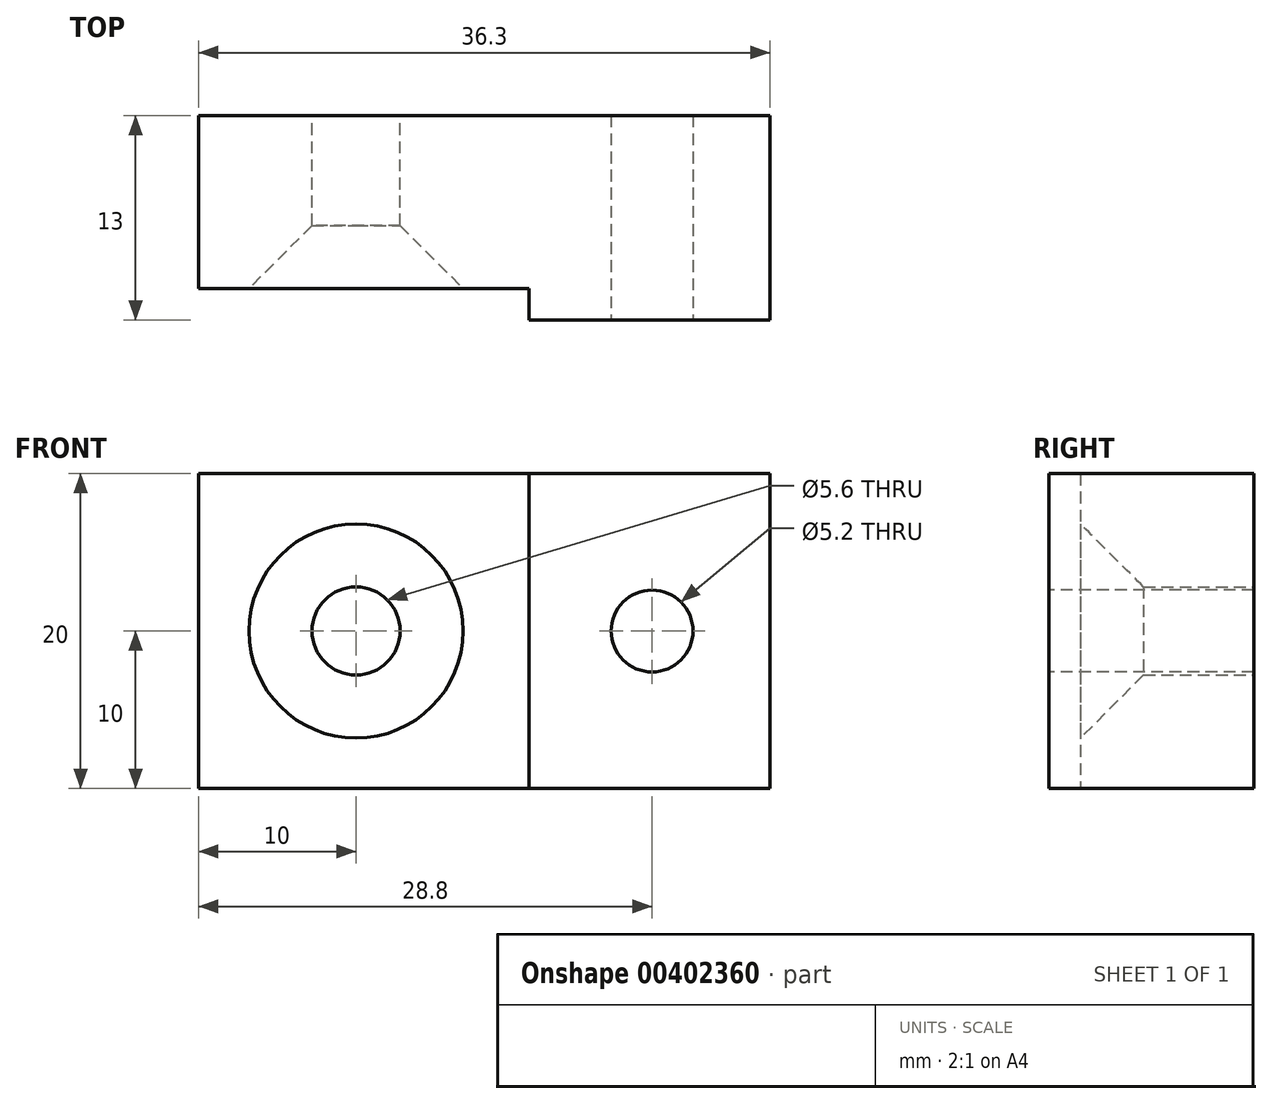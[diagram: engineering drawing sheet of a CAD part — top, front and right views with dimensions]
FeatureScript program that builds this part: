
annotation { "Feature Type Name" : "Feature", "Feature Type Description" : "" }
export const myFeature = defineFeature(function(context is Context, id is Id, definition is map)
    precondition{}
    {
        {
            var Q0;
            Q0=qCreatedBy(makeId("Top.planeOp"),FACE);
            var sketch = newSketch(context, id + "F0", { "sketchPlane" : qUnion([Q0])});
            skLineSegment(sketch, "E0", {"start": v(0, 20) * mm, "end": v(20, 20) * mm});
            skLineSegment(sketch, "E1", {"start": v(20, 20) * mm, "end": v(20, 31) * mm});
            skLineSegment(sketch, "E2", {"start": v(0, 20) * mm, "end": v(0, 31) * mm});
            skLineSegment(sketch, "E3", {"start": v(0, 31) * mm, "end": v(20, 31) * mm});
            skSolve(sketch);
        }
        {
            var Q0;
            Q0=makeQuery(id+"F0.imprint","IMPRINT",FACE,{"disambiguationData":[TD([[makeQuery(id+"F0.imprint","IMPRINT",EDGE,{"derivedFrom":sQuery(id+"F0.wireOp",EDGE,"xvJhXUSX-wpkq-VukB-ggIu-nVvylT8XI342")}),1.0]])]});
            var Q1;
            Q1=makeQuery(id+"F0.imprint","IMPRINT",FACE,{"disambiguationData":[TD([[makeQuery(id+"F0.imprint","IMPRINT",EDGE,{"derivedFrom":sQuery(id+"F0.wireOp",EDGE,"E0")}),1.0]])]});
            extrude(context, id + "F1", {"entities" : qUnion([Q0, Q1]), "depth" : 20 * mm});
        }
        {
            var Q0;
            Q0=makeQuery(id+"F1.opExtrude","SWEPT_FACE",FACE,{"disambiguationData":[OSD([sQuery(id+"F0.wireOp",EDGE,"E3")])]});
            var sketch = newSketch(context, id + "F2", { "sketchPlane" : qUnion([Q0])});
            skCircle(sketch, "E4", {"center": v(-10, 10) * mm, "radius": 2.8 * mm});
            skSolve(sketch);
        }
        {
            var Q0;
            Q0=makeQuery(id+"F2.imprint","IMPRINT",FACE,{"disambiguationData":[TD([[makeQuery(id+"F2.imprint","IMPRINT",EDGE,{"derivedFrom":sQuery(id+"F2.wireOp",EDGE,"E4")}),1.0]])]});
            extrude(context, id + "F3", {"entities" : qUnion([Q0]), "operationType" : NewBodyOperationType.REMOVE, "oppositeDirection" : true, "depth" : 25 * mm});
        }
        {
            var Q0;
            Q0=makeQuery(id+"F1.opExtrude","CAP_FACE",FACE,{"disambiguationData":[OSD([sQuery(id+"F0.wireOp",EDGE,"E0"),sQuery(id+"F0.wireOp",EDGE,"E1"),sQuery(id+"F0.wireOp",EDGE,"E2"),sQuery(id+"F0.wireOp",EDGE,"E3")])],"isStart":false});
            var sketch = newSketch(context, id + "F4", { "sketchPlane" : qUnion([Q0])});
            skLineSegment(sketch, "E5.top", {"start": v(21, 18) * mm, "end": v(36.3, 18) * mm});
            skLineSegment(sketch, "E5.left", {"start": v(20, 31) * mm, "end": v(20, 20) * mm});
            skLineSegment(sketch, "E5.right", {"start": v(36.3, 31) * mm, "end": v(36.3, 18) * mm});
            skLineSegment(sketch, "E6", {"start": v(20, 31) * mm, "end": v(36.3, 31) * mm});
            skLineSegment(sketch, "E7", {"start": v(20, 20) * mm, "end": v(21, 20) * mm});
            skLineSegment(sketch, "E8", {"start": v(21, 20) * mm, "end": v(21, 18) * mm});
            skSolve(sketch);
        }
        {
            var Q0;
            Q0=makeQuery(id+"F4.imprint","IMPRINT",FACE,{"disambiguationData":[TD([[makeQuery(id+"F4.imprint","IMPRINT",EDGE,{"derivedFrom":sQuery(id+"F4.wireOp",EDGE,"E5.top")}),1.0]])]});
            var Q1;
            Q1=makeQuery(id+"F1.opExtrude","CAP_FACE",FACE,{"disambiguationData":[OSD([sQuery(id+"F0.wireOp",EDGE,"E0"),sQuery(id+"F0.wireOp",EDGE,"E1"),sQuery(id+"F0.wireOp",EDGE,"E2"),sQuery(id+"F0.wireOp",EDGE,"E3")])],"isStart":true});
            extrude(context, id + "F5", {"entities" : qUnion([Q0]), "operationType" : NewBodyOperationType.ADD, "endBound" : BoundingType.UP_TO_SURFACE, "oppositeDirection" : true, "endBoundEntityFace" : qUnion([Q1]), "depth" : 6 * mm});
        }
        {
            var Q0;
            Q0=makeQuery(id+"F5.opExtrude","SWEPT_FACE",FACE,{"disambiguationData":[OSD([sQuery(id+"F4.wireOp",EDGE,"E5.top")])]});
            var sketch = newSketch(context, id + "F6", { "sketchPlane" : qUnion([Q0])});
            skCircle(sketch, "E9", {"center": v(28.8, 10) * mm, "radius": 2.6 * mm});
            skSolve(sketch);
        }
        {
            var Q0;
            Q0=makeQuery(id+"F6.imprint","IMPRINT",FACE,{"disambiguationData":[TD([[makeQuery(id+"F6.imprint","IMPRINT",EDGE,{"derivedFrom":sQuery(id+"F6.wireOp",EDGE,"E9")}),1.0]])]});
            extrude(context, id + "F7", {"entities" : qUnion([Q0]), "operationType" : NewBodyOperationType.REMOVE, "oppositeDirection" : true, "depth" : 25 * mm});
        }
        {
            var Q0;
            Q0=makeQuery(id+"F3.boolean.opBoolean","INTERSECT",EDGE,{"derivedFrom":[makeQuery(id+"F1.opExtrude","SWEPT_FACE",FACE,{"disambiguationData":[OSD([sQuery(id+"F0.wireOp",EDGE,"E0")])]}),makeQuery(id+"F3.opExtrude","SWEPT_FACE",FACE,{"disambiguationData":[OSD([sQuery(id+"F2.wireOp",EDGE,"E4")])]})]});
            chamfer(context, id + "F8", {"entities" : qUnion([Q0]), "width" : 4 * mm, "tangentPropagation" : true});
        }
    });
